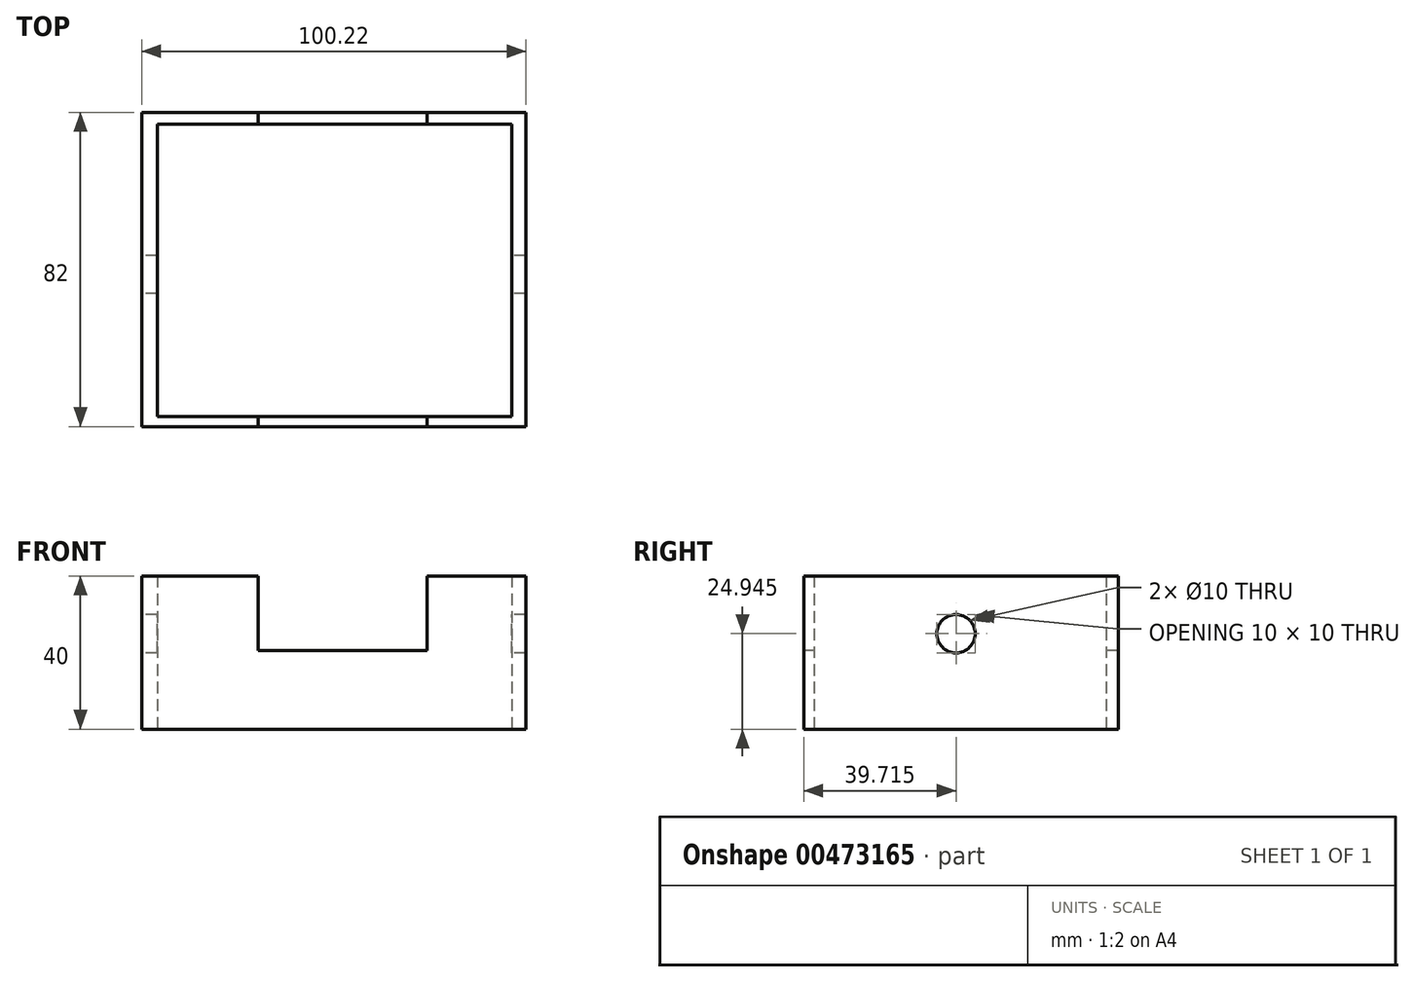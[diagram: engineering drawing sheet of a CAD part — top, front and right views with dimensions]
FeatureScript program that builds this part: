
annotation { "Feature Type Name" : "Feature", "Feature Type Description" : "" }
export const myFeature = defineFeature(function(context is Context, id is Id, definition is map)
    precondition{}
    {
        {
            var Q0;
            Q0=qCreatedBy(makeId("Top.planeOp"),FACE);
            var sketch = newSketch(context, id + "F0", { "sketchPlane" : qUnion([Q0])});
            skLineSegment(sketch, "E0.bottom", {"start": v(-45.26, -35.07) * mm, "end": v(54.96, -35.07) * mm});
            skLineSegment(sketch, "E0.top", {"start": v(-45.26, 46.93) * mm, "end": v(54.96, 46.93) * mm});
            skLineSegment(sketch, "E0.left", {"start": v(-45.26, -35.07) * mm, "end": v(-45.26, 46.93) * mm});
            skLineSegment(sketch, "E0.right", {"start": v(54.96, -35.07) * mm, "end": v(54.96, 46.93) * mm});
            skSolve(sketch);
        }
        {
            var Q0;
            Q0=qCreatedBy(makeId("Front.planeOp"),FACE);
            var sketch = newSketch(context, id + "F1", { "sketchPlane" : qUnion([Q0])});
            skLineSegment(sketch, "E1.bottom", {"start": v(-14.9, 53.39) * mm, "end": v(29.2, 53.39) * mm});
            skLineSegment(sketch, "E1.top", {"start": v(-14.9, 20.58) * mm, "end": v(29.2, 20.58) * mm});
            skLineSegment(sketch, "E1.left", {"start": v(-14.9, 53.39) * mm, "end": v(-14.9, 20.58) * mm});
            skLineSegment(sketch, "E1.right", {"start": v(29.2, 53.39) * mm, "end": v(29.2, 20.58) * mm});
            skSolve(sketch);
        }
        {
            var Q0;
            Q0=qCreatedBy(makeId("Right.planeOp"),FACE);
            var sketch = newSketch(context, id + "F2", { "sketchPlane" : qUnion([Q0])});
            skCircle(sketch, "E2", {"center": v(4.64, 24.94) * mm, "radius": 6.94 * mm});
            skSolve(sketch);
        }
        {
            var Q0;
            Q0=makeQuery(id+"F0.imprint","IMPRINT",FACE,{"disambiguationData":[TD([[makeQuery(id+"F0.imprint","IMPRINT",EDGE,{"derivedFrom":sQuery(id+"F0.wireOp",EDGE,"E0.bottom")}),1.0]])]});
            extrude(context, id + "F3", {"entities" : qUnion([Q0]), "depth" : 40 * mm});
        }
        {
            var Q0;
            Q0=sQuery(id+"F2.wireOp",VERTEX,"E2.center");
            var Q1;
            Q1=makeQuery(id+"F3.opExtrude","SWEPT_BODY",BODY,{"disambiguationData":[OSD([sQuery(id+"F0.wireOp",EDGE,"E0.bottom"),sQuery(id+"F0.wireOp",EDGE,"E0.top"),sQuery(id+"F0.wireOp",EDGE,"E0.left"),sQuery(id+"F0.wireOp",EDGE,"E0.right")])]});
            hole(context, id + "F4", {"style" : HoleStyle.SIMPLE, "endStyle" : HoleEndStyle.THROUGH, "oppositeDirection" : true, "holeDiameter" : 10 * mm, "isTappedThrough" : true, "tappedDepth" : 12 * mm, "tapClearance" : 3, "locations" : qUnion([Q0]), "scope" : qUnion([Q1])});
        }
        {
            var Q0;
            Q0=sQuery(id+"F2.wireOp",VERTEX,"E2.center");
            var Q1;
            Q1=makeQuery(id+"F3.opExtrude","SWEPT_BODY",BODY,{"disambiguationData":[OSD([sQuery(id+"F0.wireOp",EDGE,"E0.bottom"),sQuery(id+"F0.wireOp",EDGE,"E0.top"),sQuery(id+"F0.wireOp",EDGE,"E0.left"),sQuery(id+"F0.wireOp",EDGE,"E0.right")])]});
            hole(context, id + "F5", {"style" : HoleStyle.SIMPLE, "endStyle" : HoleEndStyle.THROUGH, "holeDiameter" : 10 * mm, "isTappedThrough" : true, "tappedDepth" : 12 * mm, "tapClearance" : 3, "locations" : qUnion([Q0]), "scope" : qUnion([Q1])});
        }
        {
            var Q0;
            Q0=makeQuery(id+"F1.imprint","IMPRINT",FACE,{"disambiguationData":[TD([[makeQuery(id+"F1.imprint","IMPRINT",EDGE,{"derivedFrom":sQuery(id+"F1.wireOp",EDGE,"E1.bottom")}),-1.0]])]});
            extrude(context, id + "F6", {"entities" : qUnion([Q0]), "operationType" : NewBodyOperationType.REMOVE, "oppositeDirection" : true, "depth" : 60.3 * mm, "hasSecondDirection" : true, "secondDirectionOppositeDirection" : false, "secondDirectionDepth" : 51.5 * mm});
        }
        {
            var Q0;
            Q0=qCreatedBy(makeId("Top.planeOp"),FACE);
            var sketch = newSketch(context, id + "F7", { "sketchPlane" : qUnion([Q0])});
            skLineSegment(sketch, "E3.bottom", {"start": v(-41.25, 43.88) * mm, "end": v(51.25, 43.88) * mm});
            skLineSegment(sketch, "E3.top", {"start": v(-41.25, -32.38) * mm, "end": v(51.25, -32.38) * mm});
            skLineSegment(sketch, "E3.left", {"start": v(-41.25, 43.88) * mm, "end": v(-41.25, -32.38) * mm});
            skLineSegment(sketch, "E3.right", {"start": v(51.25, 43.88) * mm, "end": v(51.25, -32.38) * mm});
            skSolve(sketch);
        }
        {
            var Q0;
            Q0=makeQuery(id+"F7.imprint","IMPRINT",FACE,{"disambiguationData":[TD([[makeQuery(id+"F7.imprint","IMPRINT",EDGE,{"derivedFrom":sQuery(id+"F7.wireOp",EDGE,"E3.bottom")}),-1.0]])]});
            extrude(context, id + "F8", {"entities" : qUnion([Q0]), "operationType" : NewBodyOperationType.REMOVE, "depth" : 52.4 * mm, "hasSecondDirection" : true, "secondDirectionOppositeDirection" : true, "secondDirectionDepth" : 25 * mm});
        }
    });
